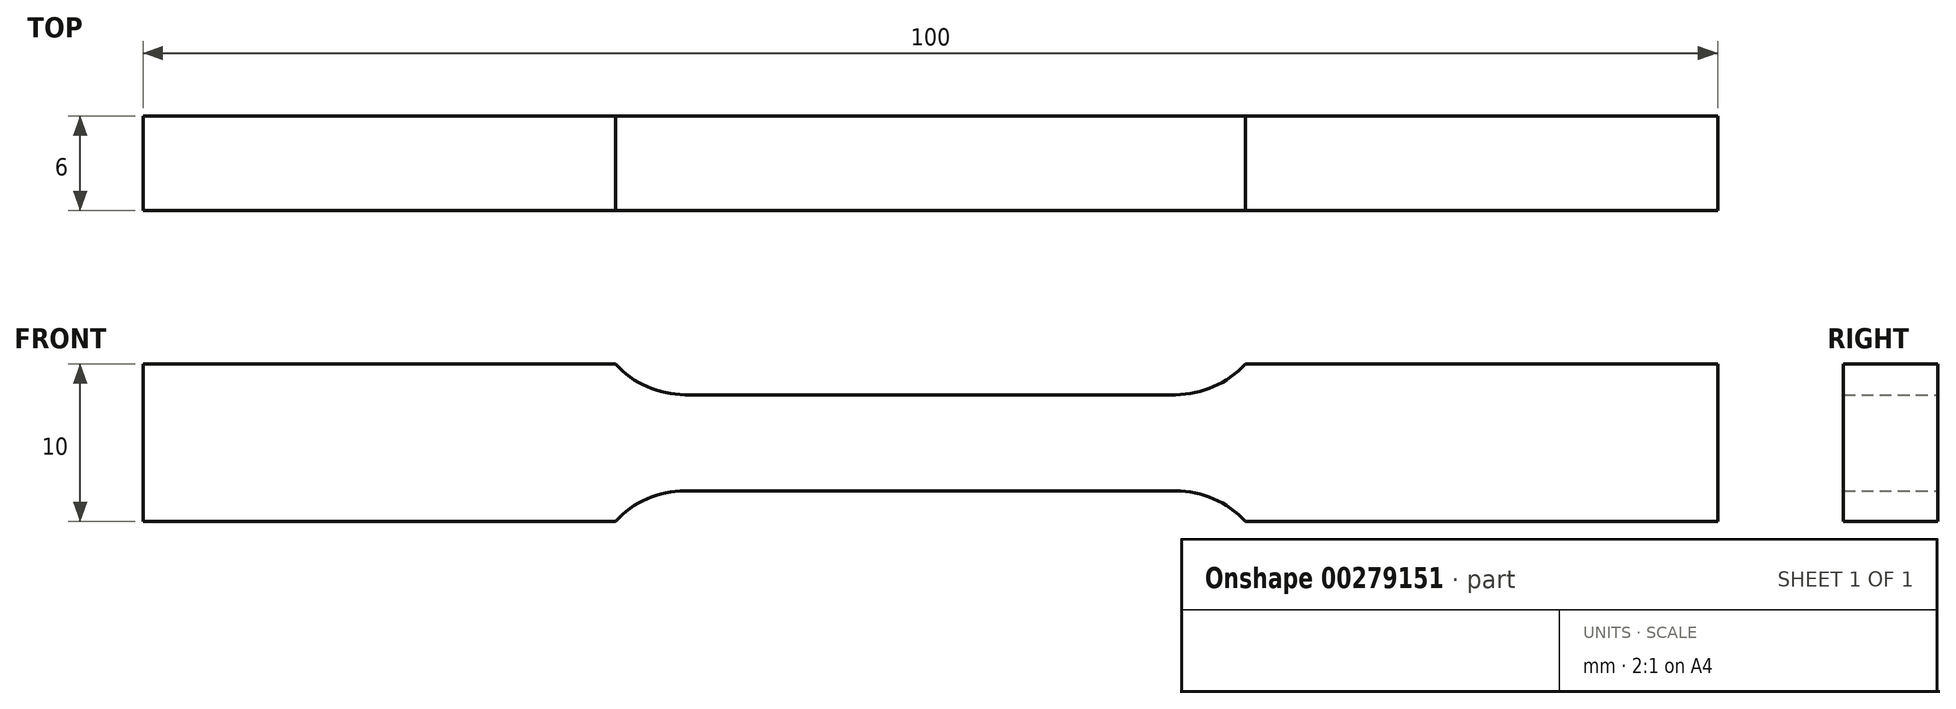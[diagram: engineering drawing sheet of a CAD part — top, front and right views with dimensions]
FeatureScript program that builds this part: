
annotation { "Feature Type Name" : "Feature", "Feature Type Description" : "" }
export const myFeature = defineFeature(function(context is Context, id is Id, definition is map)
    precondition{}
    {
        {
            var Q0;
            Q0=qCreatedBy(makeId("Front.planeOp"),FACE);
            var sketch = newSketch(context, id + "F0", { "sketchPlane" : qUnion([Q0])});
            skLineSegment(sketch, "E0", {"start": v(0, 3.05) * mm, "end": v(15.57, 3.05) * mm});
            skArc(sketch, "E1", {"start": v(15.57, 3.05) * mm, "mid": v(18, 3.56) * mm, "end": v(20, 5) * mm});
            skLineSegment(sketch, "E2", {"start": v(20, 5) * mm, "end": v(50, 5) * mm});
            skLineSegment(sketch, "E3", {"start": v(50, 5) * mm, "end": v(50, 0) * mm});
            skLineSegment(sketch, "E4.MirrorCS", {"start": v(0, -3.05) * mm, "end": v(15.57, -3.05) * mm});
            skLineSegment(sketch, "E5.MirrorCS", {"start": v(50, -5) * mm, "end": v(50, 0) * mm});
            skLineSegment(sketch, "E6.MirrorCS", {"start": v(20, -5) * mm, "end": v(50, -5) * mm});
            skArc(sketch, "E7.MirrorCS", {"start": v(15.57, -3.05) * mm, "mid": v(18, -3.56) * mm, "end": v(20, -5) * mm});
            skArc(sketch, "E8.MirrorCS", {"start": v(-15.57, -3.05) * mm, "mid": v(-18, -3.56) * mm, "end": v(-20, -5) * mm});
            skLineSegment(sketch, "E9.MirrorCS", {"start": v(-20, -5) * mm, "end": v(-50, -5) * mm});
            skArc(sketch, "E10.MirrorCS", {"start": v(-15.57, 3.05) * mm, "mid": v(-18, 3.56) * mm, "end": v(-20, 5) * mm});
            skLineSegment(sketch, "E11.MirrorCS", {"start": v(-20, 5) * mm, "end": v(-50, 5) * mm});
            skLineSegment(sketch, "E12.MirrorCS", {"start": v(-50, -5) * mm, "end": v(-50, 0) * mm});
            skLineSegment(sketch, "E13.MirrorCS", {"start": v(0, -3.05) * mm, "end": v(-15.57, -3.05) * mm});
            skLineSegment(sketch, "E14.MirrorCS", {"start": v(-50, 5) * mm, "end": v(-50, 0) * mm});
            skLineSegment(sketch, "E15.MirrorCS", {"start": v(0, 3.05) * mm, "end": v(-15.57, 3.05) * mm});
            skSolve(sketch);
        }
        {
            var Q0;
            Q0 = qSketchRegion(id + "F0", true);
            extrude(context, id + "F1", {"entities" : qUnion([Q0]), "endBound" : BoundingType.SYMMETRIC, "depth" : 6 * mm});
        }
    });
